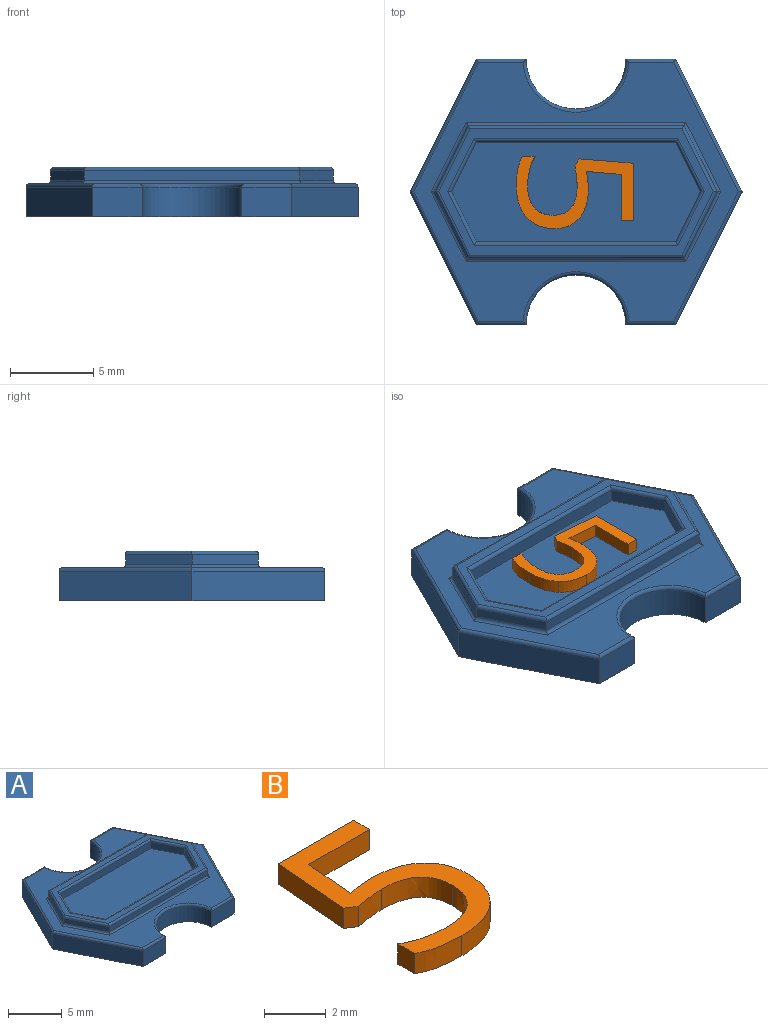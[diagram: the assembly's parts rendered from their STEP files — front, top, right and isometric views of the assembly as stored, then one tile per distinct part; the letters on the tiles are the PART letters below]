
ASSEMBLY  parts=2 mates=1
PART A: 54 faces, bbox 20x16x3 mm
  f0: cylinder r=3mm len=6mm, axis (0,0,-1), area 17mm2, adj f1,f9,f11,f46
  f1: plane 3x1.8mm, normal (0,1,0), area 5.4mm2, adj f0,f2,f11,f44
  f2: plane 8x4mm, normal (-0.89,0.45,0), area 16.1mm2, adj f1,f3,f11,f45
  f3: plane 8x4mm, normal (-0.89,-0.45,0), area 16.1mm2, adj f2,f4,f11,f47
  f4: plane 3x1.8mm, normal (0,-1,0), area 5.4mm2, adj f3,f5,f11,f49
  f5: cylinder r=3mm len=6mm, axis (0,0,-1), area 17mm2, adj f4,f6,f11,f51
  f6: plane 3x1.8mm, normal (0,-1,0), area 5.4mm2, adj f5,f7,f11,f53
  f7: plane 8x4mm, normal (0.89,-0.45,0), area 16.1mm2, adj f6,f8,f11,f52
  f8: plane 8x4mm, normal (0.89,0.45,0), area 16.1mm2, adj f7,f9,f11,f50
  f9: plane 3x1.8mm, normal (0,1,0), area 5.4mm2, adj f0,f8,f11,f48
  f10: plane 19.55x15.6mm, normal (0,0,1), area 85.7mm2, adj f26,f27,f28,f29,f30,f31,f44,f45
  f11: plane 20x16mm, normal (0,0,-1), area 227.7mm2, adj f0,f1,f2,f3,f4,f5,f6,f7
  f12: plane 4x2mm, normal (0.89,0.45,0), area 2.7mm2, adj f13,f23,f28,f40
  f13: plane 13x0.6mm, normal (0,1,0), area 7.8mm2, adj f12,f14,f26,f38
  f14: plane 4x2mm, normal (-0.89,0.45,0), area 2.7mm2, adj f13,f15,f27,f39
  f15: plane 4x2mm, normal (-0.89,-0.45,0), area 2.7mm2, adj f14,f16,f29,f41
  f16: plane 13x0.6mm, normal (0,-1,0), area 7.8mm2, adj f15,f23,f31,f43
  f17: plane 12x0.8mm, normal (0,-1,0), area 9.6mm2, adj f18,f22,f25,f35
  f18: plane 3x1.5mm, normal (-0.89,-0.45,0), area 2.7mm2, adj f17,f19,f25,f37
  f19: plane 3x1.5mm, normal (-0.89,0.45,0), area 2.7mm2, adj f18,f20,f25,f36
  f20: plane 12x0.8mm, normal (0,1,0), area 9.6mm2, adj f19,f21,f25,f34
  f21: plane 3x1.5mm, normal (0.89,0.45,0), area 2.7mm2, adj f20,f22,f25,f32
  f22: plane 3x1.5mm, normal (0.89,-0.45,0), area 2.7mm2, adj f17,f21,f25,f33
  f23: plane 4x2mm, normal (0.89,-0.45,0), area 2.7mm2, adj f12,f16,f30,f42
  f24: plane 16.55x7.6mm, normal (0,0,1), area 22.7mm2, adj f32,f33,f34,f35,f36,f37,f38,f39
  f25: plane 15x6mm, normal (0,0,1), area 81mm2, adj f17,f18,f19,f20,f21,f22
  f26: cylinder r=0.2mm len=13.25mm, axis (-1,0,0), area 4.1mm2, adj f10,f13,f27,f28
  f27: cylinder r=0.2mm len=4.29mm, axis (-0.45,-0.89,0), area 1.4mm2, adj f10,f14,f26,f29
  f28: cylinder r=0.2mm len=4.29mm, axis (-0.45,0.89,0), area 1.4mm2, adj f10,f12,f26,f30
  f29: cylinder r=0.2mm len=4.29mm, axis (0.45,-0.89,0), area 1.4mm2, adj f10,f15,f27,f31
  f30: cylinder r=0.2mm len=4.29mm, axis (0.45,0.89,0), area 1.4mm2, adj f10,f23,f28,f31
  f31: cylinder r=0.2mm len=13.25mm, axis (1,0,0), area 4.1mm2, adj f10,f16,f29,f30
  f32: cylinder r=0.2mm len=3.29mm, axis (0.45,-0.89,0), area 1.1mm2, adj f21,f24,f33,f34
  f33: cylinder r=0.2mm len=3.29mm, axis (-0.45,-0.89,0), area 1.1mm2, adj f22,f24,f32,f35
  f34: cylinder r=0.2mm len=12.25mm, axis (1,0,0), area 3.8mm2, adj f20,f24,f32,f36
  f35: cylinder r=0.2mm len=12.25mm, axis (-1,0,0), area 3.8mm2, adj f17,f24,f33,f37
  f36: cylinder r=0.2mm len=3.29mm, axis (0.45,0.89,0), area 1.1mm2, adj f19,f24,f34,f37
  f37: cylinder r=0.2mm len=3.29mm, axis (-0.45,0.89,0), area 1.1mm2, adj f18,f24,f35,f36
  f38: cylinder r=0.2mm len=13mm, axis (1,0,0), area 4.1mm2, adj f13,f24,f39,f40
  f39: cylinder r=0.2mm len=4.09mm, axis (0.45,0.89,0), area 1.4mm2, adj f14,f24,f38,f41
  f40: cylinder r=0.2mm len=4.09mm, axis (0.45,-0.89,0), area 1.4mm2, adj f12,f24,f38,f42
  f41: cylinder r=0.2mm len=4.09mm, axis (-0.45,0.89,0), area 1.4mm2, adj f15,f24,f39,f43
  f42: cylinder r=0.2mm len=4.09mm, axis (-0.45,-0.89,0), area 1.4mm2, adj f23,f24,f40,f43
  f43: cylinder r=0.2mm len=13mm, axis (-1,0,0), area 4.1mm2, adj f16,f24,f41,f42
  f44: cylinder r=0.2mm len=3mm, axis (1,0,0), area 0.9mm2, adj f1,f10,f45,f46
  f45: cylinder r=0.2mm len=8.09mm, axis (0.45,0.89,0), area 2.8mm2, adj f2,f10,f44,f47
  f46: torus R=3.2mm, axis (0,0,1), area 3mm2, adj f0,f10,f44,f48
  f47: cylinder r=0.2mm len=8.09mm, axis (-0.45,0.89,0), area 2.8mm2, adj f3,f10,f45,f49
  f48: cylinder r=0.2mm len=3mm, axis (1,0,0), area 0.9mm2, adj f9,f10,f46,f50
  f49: cylinder r=0.2mm len=3mm, axis (-1,0,0), area 0.9mm2, adj f4,f10,f47,f51
  f50: cylinder r=0.2mm len=8.09mm, axis (0.45,-0.89,0), area 2.8mm2, adj f8,f10,f48,f52
  f51: torus R=3.2mm, axis (0,0,1), area 3mm2, adj f5,f10,f49,f53
  f52: cylinder r=0.2mm len=8.09mm, axis (-0.45,-0.89,0), area 2.8mm2, adj f7,f10,f50,f53
  f53: cylinder r=0.2mm len=3mm, axis (-1,0,0), area 0.9mm2, adj f6,f10,f51,f52
PART B: 21 faces, bbox 4.4x7x0.8 mm
  f0: extruded ~1.73x0.8mm, area 1.5mm2, adj f1,f18,f19,f20
  f1: extruded ~1.09x0.8mm, area 0.9mm2, adj f0,f2,f19,f20
  f2: plane 2.08x0.8mm, normal (1,-0.08,0), area 1.7mm2, adj f1,f3,f19,f20
  f3: plane 2.78x0.8mm, normal (0,-1,0), area 2.2mm2, adj f2,f4,f19,f20
  f4: plane 0.8x0.73mm, normal (1,0,0), area 0.6mm2, adj f3,f5,f19,f20
  f5: plane 3.45x0.8mm, normal (0,1,0), area 2.8mm2, adj f4,f6,f19,f20
  f6: plane 3.25x0.8mm, normal (-1,0.08,0), area 2.6mm2, adj f5,f7,f19,f20
  f7: plane 0.8x0.41mm, normal (-0.54,-0.84,0), area 0.4mm2, adj f6,f8,f19,f20
  f8: extruded ~1.21x0.8mm, area 1mm2, adj f7,f9,f19,f20
  f9: extruded ~1.78x1.45mm, area 2.1mm2, adj f8,f10,f19,f20
  f10: extruded ~1.14x0.8mm, area 1mm2, adj f9,f11,f19,f20
  f11: extruded ~1.3x0.8mm, area 1.1mm2, adj f10,f12,f19,f20
  f12: extruded ~0.97x0.8mm, area 0.8mm2, adj f11,f13,f19,f20
  f13: extruded ~0.83x0.8mm, area 0.7mm2, adj f12,f14,f19,f20
  f14: plane 0.8x0.76mm, normal (-1,0,0), area 0.6mm2, adj f13,f15,f19,f20
  f15: extruded ~1.79x0.8mm, area 1.5mm2, adj f14,f16,f19,f20
  f16: extruded ~1.89x0.8mm, area 1.6mm2, adj f15,f17,f19,f20
  f17: extruded ~1.69x0.8mm, area 1.5mm2, adj f16,f18,f19,f20
  f18: extruded ~1.49x0.8mm, area 1.3mm2, adj f0,f17,f19,f20
  f19: plane 7.04x4.37mm, normal (0,0,1), area 11.2mm2, adj f0,f1,f2,f3,f4,f5,f6,f7
  f20: plane 7.04x4.37mm, normal (0,0,-1), area 11.2mm2, adj f0,f1,f2,f3,f4,f5,f6,f7
PLACE A at identity
PLACE B rot(axis=(0,0,-1),90deg) t=(0.23,-0.02,2)mm
MATE parallel B.f20 <-> A.f25  axis (0,0,-1) through (0,0,2)mm
